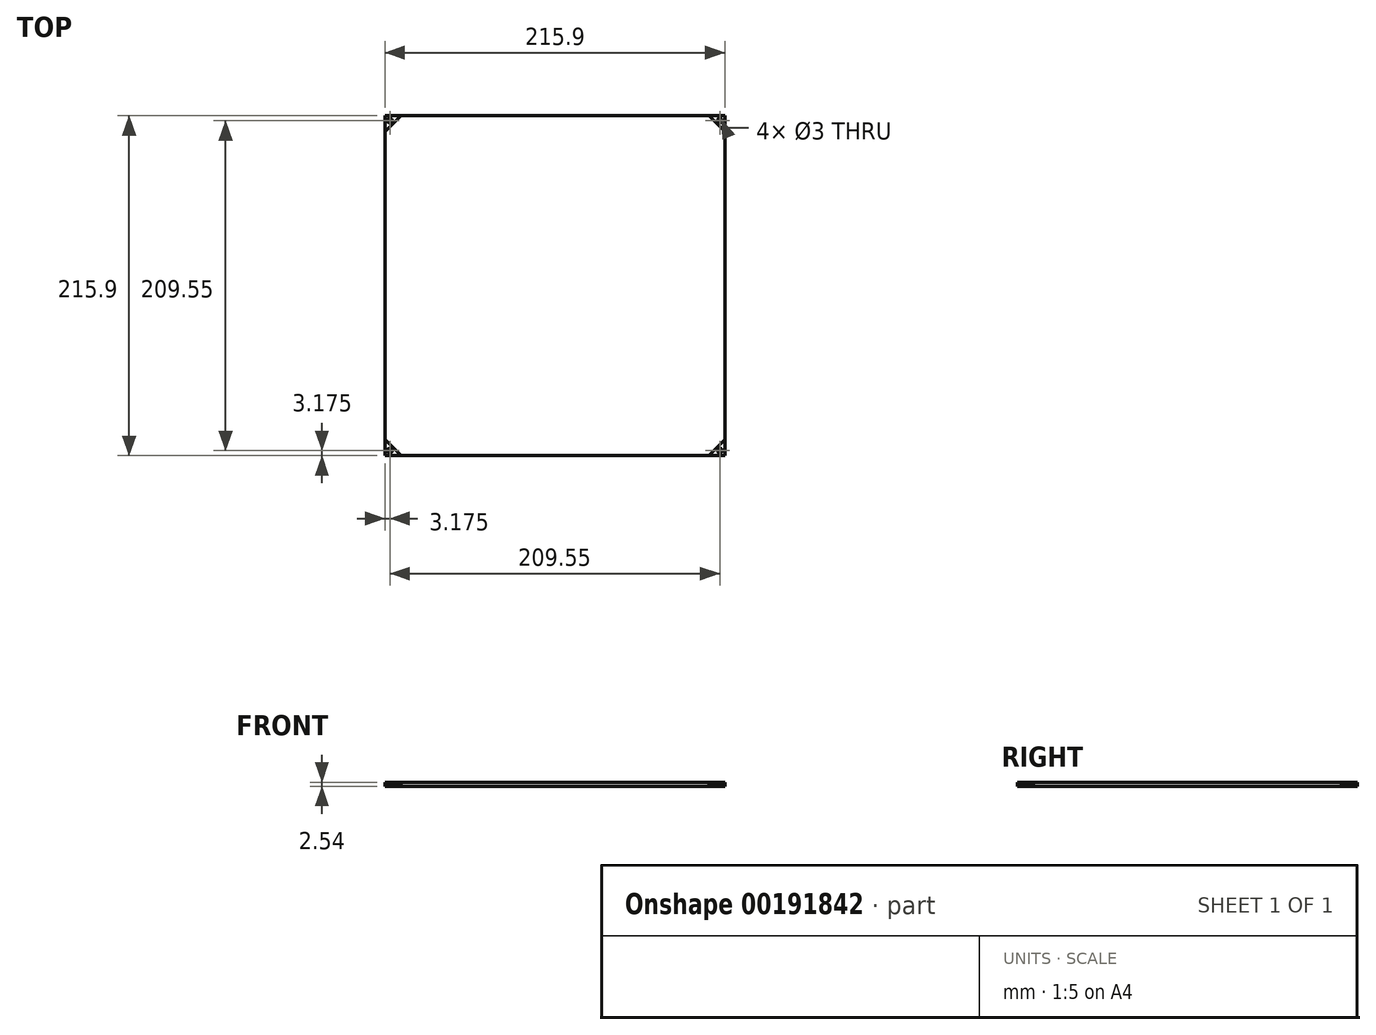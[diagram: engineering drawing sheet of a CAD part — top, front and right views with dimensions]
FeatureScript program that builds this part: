
annotation { "Feature Type Name" : "Feature", "Feature Type Description" : "" }
export const myFeature = defineFeature(function(context is Context, id is Id, definition is map)
    precondition{}
    {
        {
            var Q0;
            Q0=qCreatedBy(makeId("Top.planeOp"),FACE);
            var sketch = newSketch(context, id + "F0", { "sketchPlane" : qUnion([Q0])});
            skLineSegment(sketch, "E0.bottom", {"start": v(107.95, -107.95) * mm, "end": v(-107.95, -107.95) * mm});
            skLineSegment(sketch, "E0.top", {"start": v(107.95, 107.95) * mm, "end": v(-107.95, 107.95) * mm});
            skLineSegment(sketch, "E0.left", {"start": v(107.95, -107.95) * mm, "end": v(107.95, 107.95) * mm});
            skLineSegment(sketch, "E0.right", {"start": v(-107.95, -107.95) * mm, "end": v(-107.95, 107.95) * mm});
            skPoint(sketch, "E0.middle", {"position": v(0, 0) * mm});
            skSolve(sketch);
        }
        {
            var Q0;
            Q0 = qSketchRegion(id + "F0", true);
            extrude(context, id + "F1", {"entities" : qUnion([Q0]), "oppositeDirection" : true, "depth" : 2.54 * mm});
        }
        {
            var Q0;
            Q0=makeQuery(id+"F1.opExtrude","CAP_FACE",FACE,{"disambiguationData":[OSD([sQuery(id+"F0.wireOp",EDGE,"E0.bottom"),sQuery(id+"F0.wireOp",EDGE,"E0.top"),sQuery(id+"F0.wireOp",EDGE,"E0.left"),sQuery(id+"F0.wireOp",EDGE,"E0.right")])],"isStart":true});
            var sketch = newSketch(context, id + "F2", { "sketchPlane" : qUnion([Q0])});
            skLineSegment(sketch, "E1", {"start": v(-107.95, 97.8) * mm, "end": v(-97.79, 107.95) * mm});
            skLineSegment(sketch, "E2", {"start": v(-107.95, 97.8) * mm, "end": v(-107.95, 107.95) * mm});
            skLineSegment(sketch, "E3", {"start": v(-107.95, 107.95) * mm, "end": v(-97.79, 107.95) * mm});
            skLineSegment(sketch, "E4.MirrorCS", {"start": v(107.95, 107.95) * mm, "end": v(97.79, 107.95) * mm});
            skLineSegment(sketch, "E5.MirrorCS", {"start": v(107.95, 97.8) * mm, "end": v(97.79, 107.95) * mm});
            skLineSegment(sketch, "E6.MirrorCS", {"start": v(107.95, 97.8) * mm, "end": v(107.95, 107.95) * mm});
            skLineSegment(sketch, "E7.MirrorCS", {"start": v(107.95, -107.95) * mm, "end": v(97.79, -107.95) * mm});
            skLineSegment(sketch, "E8.MirrorCS", {"start": v(-107.95, -97.8) * mm, "end": v(-107.95, -107.95) * mm});
            skLineSegment(sketch, "E9.MirrorCS", {"start": v(107.95, -97.8) * mm, "end": v(107.95, -107.95) * mm});
            skLineSegment(sketch, "E10.MirrorCS", {"start": v(-107.95, -97.8) * mm, "end": v(-97.8, -107.95) * mm});
            skLineSegment(sketch, "E11.MirrorCS", {"start": v(-107.95, -107.95) * mm, "end": v(-97.79, -107.95) * mm});
            skLineSegment(sketch, "E12.MirrorCS", {"start": v(107.95, -97.8) * mm, "end": v(97.8, -107.95) * mm});
            skSolve(sketch);
        }
        {
            var Q0;
            Q0 = qSketchRegion(id + "F2", true);
            extrude(context, id + "F3", {"entities" : qUnion([Q0]), "operationType" : NewBodyOperationType.REMOVE, "oppositeDirection" : true, "depth" : 1.27 * mm});
        }
        {
            var Q0;
            Q0=makeQuery(id+"F3.boolean.opBoolean","COPY",FACE,{"derivedFrom":makeQuery(id+"F3.opExtrude","CAP_FACE",FACE,{"disambiguationData":[OSD([sQuery(id+"F2.wireOp",EDGE,"E7.MirrorCS"),sQuery(id+"F2.wireOp",EDGE,"E9.MirrorCS"),sQuery(id+"F2.wireOp",EDGE,"E12.MirrorCS")])],"isStart":false})});
            var sketch = newSketch(context, id + "F4", { "sketchPlane" : qUnion([Q0])});
            skLineSegment(sketch, "E13.bottom", {"start": v(107.95, -107.95) * mm, "end": v(104.78, -107.95) * mm, "construction": true});
            skLineSegment(sketch, "E13.top", {"start": v(107.95, -104.77) * mm, "end": v(104.78, -104.77) * mm, "construction": true});
            skLineSegment(sketch, "E13.left", {"start": v(107.95, -107.95) * mm, "end": v(107.95, -104.77) * mm, "construction": true});
            skLineSegment(sketch, "E13.right", {"start": v(104.78, -107.95) * mm, "end": v(104.78, -104.77) * mm, "construction": true});
            skPoint(sketch, "E14", {"position": v(104.78, -104.77) * mm});
            skPoint(sketch, "E15.MirrorP", {"position": v(-104.78, -104.77) * mm});
            skPoint(sketch, "E16.MirrorP", {"position": v(-104.78, 104.77) * mm});
            skPoint(sketch, "E17.MirrorP", {"position": v(104.78, 104.77) * mm});
            skCircle(sketch, "E18", {"center": v(104.78, -104.77) * mm, "radius": 2.85 * mm, "construction": true});
            skSolve(sketch);
        }
        {
            var Q0;
            Q0=sQuery(id+"F4.wireOp",VERTEX,"E14");
            var Q1;
            Q1=sQuery(id+"F4.wireOp",VERTEX,"E15.MirrorP");
            var Q2;
            Q2=sQuery(id+"F4.wireOp",VERTEX,"E16.MirrorP");
            var Q3;
            Q3=sQuery(id+"F4.wireOp",VERTEX,"E17.MirrorP");
            var Q4;
            Q4=makeQuery(id+"F1.opExtrude","SWEPT_BODY",BODY,{"disambiguationData":[OSD([sQuery(id+"F0.wireOp",EDGE,"E0.bottom"),sQuery(id+"F0.wireOp",EDGE,"E0.top"),sQuery(id+"F0.wireOp",EDGE,"E0.left"),sQuery(id+"F0.wireOp",EDGE,"E0.right")])]});
            hole(context, id + "F5", {"style" : HoleStyle.SIMPLE, "endStyle" : HoleEndStyle.THROUGH, "holeDiameter" : 3 * mm, "locations" : qUnion([Q0, Q1, Q2, Q3]), "scope" : qUnion([Q4]), "isTappedThrough" : true});
        }
    });
